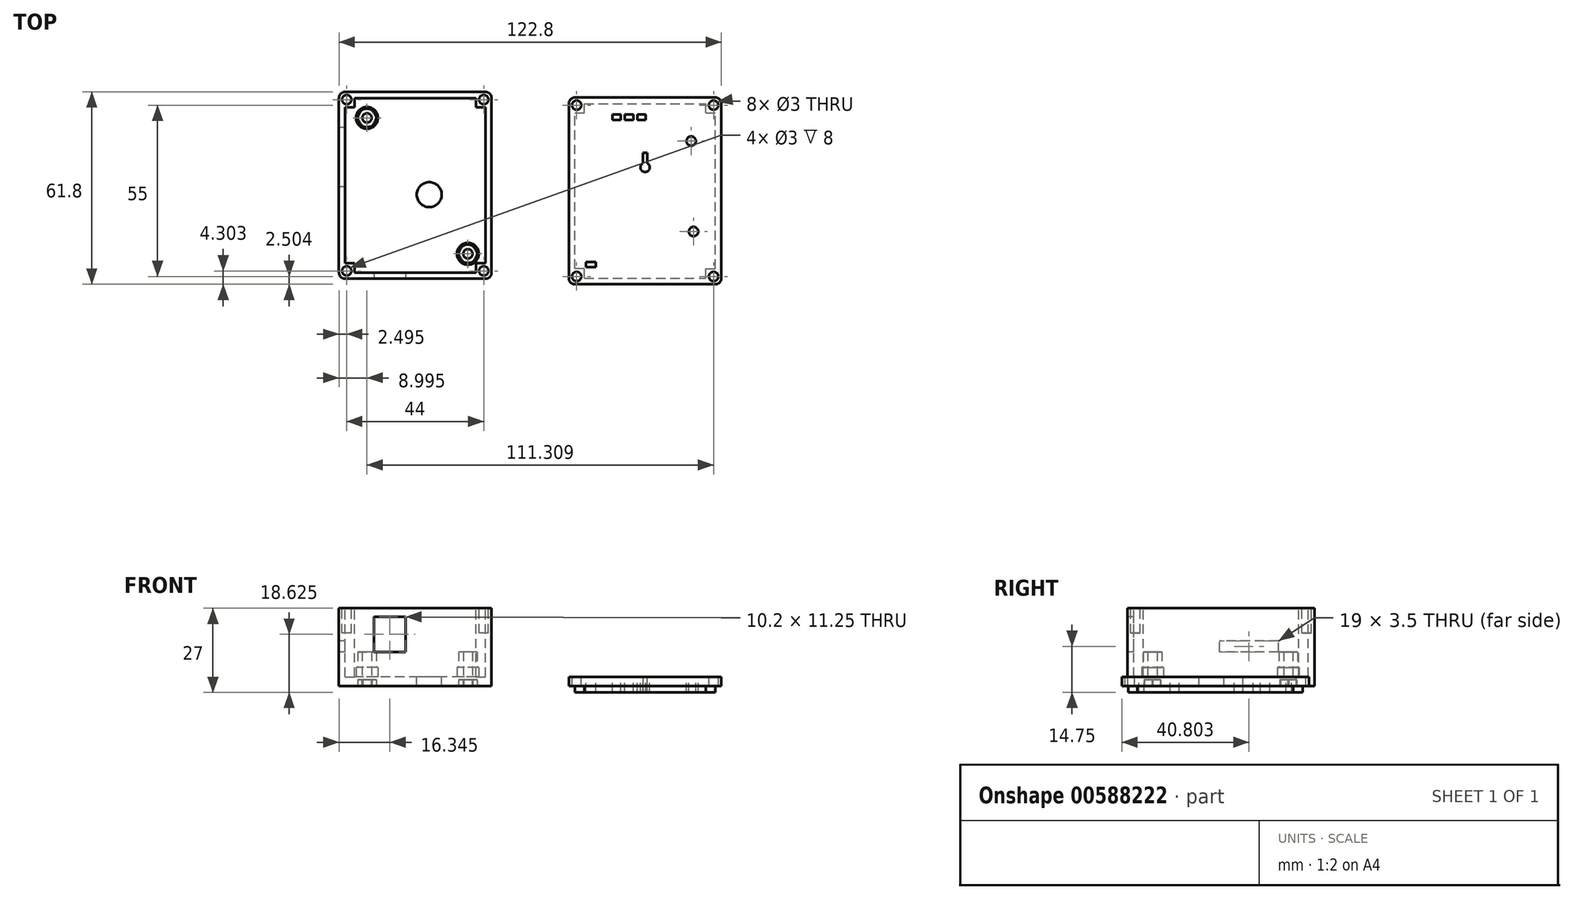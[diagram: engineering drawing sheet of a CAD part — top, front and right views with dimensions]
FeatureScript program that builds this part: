
annotation { "Feature Type Name" : "Feature", "Feature Type Description" : "" }
export const myFeature = defineFeature(function(context is Context, id is Id, definition is map)
    precondition{}
    {
        {
            var Q0;
            Q0=qCreatedBy(makeId("Top.planeOp"),FACE);
            var sketch = newSketch(context, id + "F0", { "sketchPlane" : qUnion([Q0])});
            skLineSegment(sketch, "E0.bottom", {"start": v(-66.77, 67.35) * mm, "end": v(-17.77, 67.35) * mm});
            skLineSegment(sketch, "E0.top", {"start": v(-66.77, 7.35) * mm, "end": v(-17.77, 7.35) * mm});
            skLineSegment(sketch, "E0.left", {"start": v(-66.77, 67.35) * mm, "end": v(-66.77, 7.35) * mm});
            skLineSegment(sketch, "E0.right", {"start": v(-17.77, 67.35) * mm, "end": v(-17.77, 7.35) * mm});
            skPoint(sketch, "E1.middle", {"position": v(-42.27, 37.35) * mm});
            skPoint(sketch, "E1.middle.positionSnap0", {"position": v(-66.77, 37.35) * mm});
            skPoint(sketch, "E1.middle.positionSnap1", {"position": v(-42.27, 67.35) * mm});
            skPoint(sketch, "E1.centerSnap0", {"position": v(-66.77, 37.35) * mm});
            skPoint(sketch, "E1.centerSnap1", {"position": v(-42.27, 67.35) * mm});
            skSolve(sketch);
        }
        {
            var Q0;
            Q0=makeQuery(id+"F0.imprint","IMPRINT",FACE,{"disambiguationData":[TD([[makeQuery(id+"F0.imprint","IMPRINT",EDGE,{"derivedFrom":sQuery(id+"F0.wireOp",EDGE,"E0.bottom")}),-1.0]])]});
            extrude(context, id + "F1", {"entities" : qUnion([Q0]), "depth" : 25 * mm, "offsetDistance" : 25 * mm});
        }
        {
            var Q0;
            Q0=makeQuery(id+"F1.opExtrude","CAP_FACE",FACE,{"disambiguationData":[OSD([sQuery(id+"F0.wireOp",EDGE,"E0.bottom"),sQuery(id+"F0.wireOp",EDGE,"E0.top"),sQuery(id+"F0.wireOp",EDGE,"E0.left"),sQuery(id+"F0.wireOp",EDGE,"E0.right")])],"isStart":false});
            var sketch = newSketch(context, id + "F2", { "sketchPlane" : qUnion([Q0])});
            skLineSegment(sketch, "E2.bottom", {"start": v(-61.77, 62.35) * mm, "end": v(-22.77, 62.35) * mm});
            skLineSegment(sketch, "E2.top", {"start": v(-61.77, 12.35) * mm, "end": v(-22.77, 12.35) * mm});
            skLineSegment(sketch, "E2.left", {"start": v(-61.77, 62.35) * mm, "end": v(-61.77, 12.35) * mm});
            skLineSegment(sketch, "E2.right", {"start": v(-22.77, 62.35) * mm, "end": v(-22.77, 12.35) * mm});
            skPoint(sketch, "E2.middle", {"position": v(-42.27, 37.35) * mm});
            skPoint(sketch, "E2.middle.positionSnap0", {"position": v(-17.77, 37.35) * mm});
            skPoint(sketch, "E2.middle.positionSnap1", {"position": v(-42.27, 67.35) * mm});
            skPoint(sketch, "E2.centerSnap0", {"position": v(-17.77, 37.35) * mm});
            skPoint(sketch, "E2.centerSnap1", {"position": v(-42.27, 67.35) * mm});
            skSolve(sketch);
        }
        {
            var Q0;
            Q0=makeQuery(id+"F2.imprint","IMPRINT",FACE,{"disambiguationData":[TD([[makeQuery(id+"F2.imprint","IMPRINT",EDGE,{"derivedFrom":sQuery(id+"F2.wireOp",EDGE,"E2.bottom")}),-1.0]])]});
            extrude(context, id + "F3", {"entities" : qUnion([Q0]), "operationType" : NewBodyOperationType.REMOVE, "oppositeDirection" : true, "depth" : 22 * mm, "offsetDistance" : 25 * mm});
        }
        {
            var Q0;
            Q0=makeQuery(id+"F1.opExtrude","CAP_FACE",FACE,{"disambiguationData":[OSD([sQuery(id+"F0.wireOp",EDGE,"E0.bottom"),sQuery(id+"F0.wireOp",EDGE,"E0.top"),sQuery(id+"F0.wireOp",EDGE,"E0.left"),sQuery(id+"F0.wireOp",EDGE,"E0.right")])],"isStart":false});
            var sketch = newSketch(context, id + "F4", { "sketchPlane" : qUnion([Q0])});
            skLineSegment(sketch, "E3.bottom", {"start": v(-61.77, 12.35) * mm, "end": v(-66.77, 12.35) * mm});
            skLineSegment(sketch, "E3.top", {"start": v(-61.77, 7.35) * mm, "end": v(-66.77, 7.35) * mm});
            skLineSegment(sketch, "E3.left", {"start": v(-61.77, 12.35) * mm, "end": v(-61.77, 7.35) * mm});
            skLineSegment(sketch, "E3.right", {"start": v(-66.77, 12.35) * mm, "end": v(-66.77, 7.35) * mm});
            skLineSegment(sketch, "E4.bottom", {"start": v(-22.77, 12.35) * mm, "end": v(-17.77, 12.35) * mm});
            skLineSegment(sketch, "E4.top", {"start": v(-22.77, 7.35) * mm, "end": v(-17.77, 7.35) * mm});
            skLineSegment(sketch, "E4.left", {"start": v(-22.77, 12.35) * mm, "end": v(-22.77, 7.35) * mm});
            skLineSegment(sketch, "E4.right", {"start": v(-17.77, 12.35) * mm, "end": v(-17.77, 7.35) * mm});
            skLineSegment(sketch, "E5.bottom", {"start": v(-61.77, 62.35) * mm, "end": v(-66.77, 62.35) * mm});
            skLineSegment(sketch, "E5.top", {"start": v(-61.77, 67.35) * mm, "end": v(-66.77, 67.35) * mm});
            skLineSegment(sketch, "E5.left", {"start": v(-61.77, 62.35) * mm, "end": v(-61.77, 67.35) * mm});
            skLineSegment(sketch, "E5.right", {"start": v(-66.77, 62.35) * mm, "end": v(-66.77, 67.35) * mm});
            skLineSegment(sketch, "E6.bottom", {"start": v(-22.77, 62.35) * mm, "end": v(-17.77, 62.35) * mm});
            skLineSegment(sketch, "E6.top", {"start": v(-22.77, 67.35) * mm, "end": v(-17.77, 67.35) * mm});
            skLineSegment(sketch, "E6.left", {"start": v(-22.77, 62.35) * mm, "end": v(-22.77, 67.35) * mm});
            skLineSegment(sketch, "E6.right", {"start": v(-17.77, 62.35) * mm, "end": v(-17.77, 67.35) * mm});
            skCircle(sketch, "E7", {"center": v(-64.27, 9.85) * mm, "radius": 1.5 * mm});
            skPoint(sketch, "E7.centerSnap0", {"position": v(-61.77, 9.85) * mm});
            skPoint(sketch, "E7.centerSnap1", {"position": v(-64.27, 12.35) * mm});
            skCircle(sketch, "E8", {"center": v(-64.27, 64.85) * mm, "radius": 1.5 * mm});
            skPoint(sketch, "E8.centerSnap0", {"position": v(-64.27, 62.35) * mm});
            skPoint(sketch, "E8.centerSnap1", {"position": v(-61.77, 64.85) * mm});
            skCircle(sketch, "E9", {"center": v(-20.27, 64.85) * mm, "radius": 1.5 * mm});
            skPoint(sketch, "E9.centerSnap0", {"position": v(-20.27, 62.35) * mm});
            skPoint(sketch, "E9.centerSnap1", {"position": v(-22.77, 64.85) * mm});
            skCircle(sketch, "E10", {"center": v(-20.27, 9.85) * mm, "radius": 1.5 * mm});
            skPoint(sketch, "E10.centerSnap0", {"position": v(-22.77, 9.85) * mm});
            skPoint(sketch, "E10.centerSnap1", {"position": v(-20.27, 12.35) * mm});
            skSolve(sketch);
        }
        {
            var Q0;
            Q0=makeQuery(id+"F4.imprint","IMPRINT",FACE,{"disambiguationData":[TD([[makeQuery(id+"F4.imprint","IMPRINT",EDGE,{"derivedFrom":sQuery(id+"F4.wireOp",EDGE,"E9")}),1.0]])]});
            var Q1;
            Q1=makeQuery(id+"F4.imprint","IMPRINT",FACE,{"disambiguationData":[TD([[makeQuery(id+"F4.imprint","IMPRINT",EDGE,{"derivedFrom":sQuery(id+"F4.wireOp",EDGE,"E10")}),1.0]])]});
            var Q2;
            Q2=makeQuery(id+"F4.imprint","IMPRINT",FACE,{"disambiguationData":[TD([[makeQuery(id+"F4.imprint","IMPRINT",EDGE,{"derivedFrom":sQuery(id+"F4.wireOp",EDGE,"E7")}),1.0]])]});
            var Q3;
            Q3=makeQuery(id+"F4.imprint","IMPRINT",FACE,{"disambiguationData":[TD([[makeQuery(id+"F4.imprint","IMPRINT",EDGE,{"derivedFrom":sQuery(id+"F4.wireOp",EDGE,"E8")}),1.0]])]});
            var Q4;
            Q4 = qSketchRegion(id + "F6", true);
            extrude(context, id + "F5", {"entities" : qUnion([Q0, Q1, Q2, Q3, Q4]), "operationType" : NewBodyOperationType.REMOVE, "oppositeDirection" : true, "depth" : 8 * mm, "offsetDistance" : 25 * mm});
        }
        {
            var Q0;
            Q0=makeQuery(id+"F1.opExtrude","CAP_FACE",FACE,{"disambiguationData":[OSD([sQuery(id+"F0.wireOp",EDGE,"E0.bottom"),sQuery(id+"F0.wireOp",EDGE,"E0.top"),sQuery(id+"F0.wireOp",EDGE,"E0.left"),sQuery(id+"F0.wireOp",EDGE,"E0.right")])],"isStart":false});
            var sketch = newSketch(context, id + "F6", { "sketchPlane" : qUnion([Q0])});
            skLineSegment(sketch, "E11.bottom", {"start": v(-22.77, 65.35) * mm, "end": v(-61.77, 65.35) * mm});
            skLineSegment(sketch, "E11.top", {"start": v(-22.77, 62.35) * mm, "end": v(-61.77, 62.35) * mm});
            skLineSegment(sketch, "E11.left", {"start": v(-22.77, 65.35) * mm, "end": v(-22.77, 62.35) * mm});
            skLineSegment(sketch, "E11.right", {"start": v(-61.77, 65.35) * mm, "end": v(-61.77, 62.35) * mm});
            skLineSegment(sketch, "E12.bottom", {"start": v(-22.77, 62.35) * mm, "end": v(-19.77, 62.35) * mm});
            skLineSegment(sketch, "E12.top", {"start": v(-22.77, 12.35) * mm, "end": v(-19.77, 12.35) * mm});
            skLineSegment(sketch, "E12.left", {"start": v(-22.77, 62.35) * mm, "end": v(-22.77, 12.35) * mm});
            skLineSegment(sketch, "E12.right", {"start": v(-19.77, 62.35) * mm, "end": v(-19.77, 12.35) * mm});
            skLineSegment(sketch, "E13.bottom", {"start": v(-61.77, 62.35) * mm, "end": v(-64.77, 62.35) * mm});
            skLineSegment(sketch, "E13.top", {"start": v(-61.77, 12.35) * mm, "end": v(-64.77, 12.35) * mm});
            skLineSegment(sketch, "E13.left", {"start": v(-61.77, 62.35) * mm, "end": v(-61.77, 12.35) * mm});
            skLineSegment(sketch, "E13.right", {"start": v(-64.77, 62.35) * mm, "end": v(-64.77, 12.35) * mm});
            skLineSegment(sketch, "E14.bottom", {"start": v(-22.77, 12.35) * mm, "end": v(-61.77, 12.35) * mm});
            skLineSegment(sketch, "E14.top", {"start": v(-22.77, 9.35) * mm, "end": v(-61.77, 9.35) * mm});
            skLineSegment(sketch, "E14.left", {"start": v(-22.77, 12.35) * mm, "end": v(-22.77, 9.35) * mm});
            skLineSegment(sketch, "E14.right", {"start": v(-61.77, 12.35) * mm, "end": v(-61.77, 9.35) * mm});
            skSolve(sketch);
        }
        {
            var Q0;
            Q0=makeQuery(id+"F6.imprint","IMPRINT",FACE,{"disambiguationData":[TD([[makeQuery(id+"F6.imprint","IMPRINT",EDGE,{"derivedFrom":sQuery(id+"F6.wireOp",EDGE,"E11.bottom")}),1.0]])]});
            var Q1;
            Q1=makeQuery(id+"F6.imprint","IMPRINT",FACE,{"disambiguationData":[TD([[makeQuery(id+"F6.imprint","IMPRINT",EDGE,{"derivedFrom":sQuery(id+"F6.wireOp",EDGE,"E13.bottom")}),1.0]])]});
            var Q2;
            Q2=makeQuery(id+"F6.imprint","IMPRINT",FACE,{"disambiguationData":[TD([[makeQuery(id+"F6.imprint","IMPRINT",EDGE,{"derivedFrom":sQuery(id+"F6.wireOp",EDGE,"E14.bottom")}),-1.0]])]});
            var Q3;
            Q3=makeQuery(id+"F6.imprint","IMPRINT",FACE,{"disambiguationData":[TD([[makeQuery(id+"F6.imprint","IMPRINT",EDGE,{"derivedFrom":sQuery(id+"F6.wireOp",EDGE,"E12.bottom")}),-1.0]])]});
            extrude(context, id + "F7", {"entities" : qUnion([Q0, Q1, Q2, Q3]), "operationType" : NewBodyOperationType.REMOVE, "oppositeDirection" : true, "depth" : 22 * mm, "offsetDistance" : 25 * mm});
        }
        {
            var Q0;
            Q0=makeQuery(id+"F7.boolean.opBoolean","MERGE",FACE,{"derivedFrom":[makeQuery(id+"F3.boolean.opBoolean","COPY",FACE,{"derivedFrom":makeQuery(id+"F3.opExtrude","CAP_FACE",FACE,{"disambiguationData":[OSD([sQuery(id+"F2.wireOp",EDGE,"E2.bottom"),sQuery(id+"F2.wireOp",EDGE,"E2.top"),sQuery(id+"F2.wireOp",EDGE,"E2.left"),sQuery(id+"F2.wireOp",EDGE,"E2.right")])],"isStart":false})}),makeQuery(id+"F7.opExtrude","CAP_FACE",FACE,{"disambiguationData":[OSD([sQuery(id+"F6.wireOp",EDGE,"E11.bottom"),sQuery(id+"F6.wireOp",EDGE,"E11.top"),sQuery(id+"F6.wireOp",EDGE,"E11.left"),sQuery(id+"F6.wireOp",EDGE,"E11.right")])],"isStart":false}),makeQuery(id+"F7.opExtrude","CAP_FACE",FACE,{"disambiguationData":[OSD([sQuery(id+"F6.wireOp",EDGE,"E12.bottom"),sQuery(id+"F6.wireOp",EDGE,"E12.top"),sQuery(id+"F6.wireOp",EDGE,"E12.left"),sQuery(id+"F6.wireOp",EDGE,"E12.right")])],"isStart":false}),makeQuery(id+"F7.opExtrude","CAP_FACE",FACE,{"disambiguationData":[OSD([sQuery(id+"F6.wireOp",EDGE,"E13.bottom"),sQuery(id+"F6.wireOp",EDGE,"E13.top"),sQuery(id+"F6.wireOp",EDGE,"E13.left"),sQuery(id+"F6.wireOp",EDGE,"E13.right")])],"isStart":false}),makeQuery(id+"F7.opExtrude","CAP_FACE",FACE,{"disambiguationData":[OSD([sQuery(id+"F6.wireOp",EDGE,"E14.bottom"),sQuery(id+"F6.wireOp",EDGE,"E14.top"),sQuery(id+"F6.wireOp",EDGE,"E14.left"),sQuery(id+"F6.wireOp",EDGE,"E14.right")])],"isStart":false})]});
            var sketch = newSketch(context, id + "F8", { "sketchPlane" : qUnion([Q0])});
            skCircle(sketch, "E15", {"center": v(-57.77, 58.97) * mm, "radius": 3 * mm});
            skCircle(sketch, "E16", {"center": v(-57.77, 58.97) * mm, "radius": 1.5 * mm});
            skCircle(sketch, "E17", {"center": v(-25.37, 15.35) * mm, "radius": 1.5 * mm});
            skCircle(sketch, "E18", {"center": v(-25.37, 15.35) * mm, "radius": 3 * mm});
            skSolve(sketch);
        }
        {
            var Q0;
            Q0=makeQuery(id+"F8.imprint","IMPRINT",FACE,{"disambiguationData":[TD([[makeQuery(id+"F8.imprint","IMPRINT",EDGE,{"derivedFrom":sQuery(id+"F8.wireOp",EDGE,"E15")}),1.0]])]});
            var Q1;
            Q1=makeQuery(id+"F8.imprint","IMPRINT",FACE,{"disambiguationData":[TD([[makeQuery(id+"F8.imprint","IMPRINT",EDGE,{"derivedFrom":sQuery(id+"F8.wireOp",EDGE,"E17")}),-1.0]])]});
            extrude(context, id + "F9", {"entities" : qUnion([Q0, Q1]), "operationType" : NewBodyOperationType.ADD, "depth" : 8 * mm, "offsetDistance" : 25 * mm});
        }
        {
            var Q0;
            Q0=makeQuery(id+"F9.boolean.opBoolean","SPLIT",FACE,{"disambiguationData":[TD([makeQuery(id+"F9.opExtrude","SWEPT_FACE",FACE,{"disambiguationData":[OSD([sQuery(id+"F8.wireOp",EDGE,"E17")])]})])],"derivedFrom":makeQuery(id+"F7.boolean.opBoolean","MERGE",FACE,{"derivedFrom":[makeQuery(id+"F3.boolean.opBoolean","COPY",FACE,{"derivedFrom":makeQuery(id+"F3.opExtrude","CAP_FACE",FACE,{"disambiguationData":[OSD([sQuery(id+"F2.wireOp",EDGE,"E2.bottom"),sQuery(id+"F2.wireOp",EDGE,"E2.top"),sQuery(id+"F2.wireOp",EDGE,"E2.left"),sQuery(id+"F2.wireOp",EDGE,"E2.right")])],"isStart":false})}),makeQuery(id+"F7.opExtrude","CAP_FACE",FACE,{"disambiguationData":[OSD([sQuery(id+"F6.wireOp",EDGE,"E11.bottom"),sQuery(id+"F6.wireOp",EDGE,"E11.top"),sQuery(id+"F6.wireOp",EDGE,"E11.left"),sQuery(id+"F6.wireOp",EDGE,"E11.right")])],"isStart":false}),makeQuery(id+"F7.opExtrude","CAP_FACE",FACE,{"disambiguationData":[OSD([sQuery(id+"F6.wireOp",EDGE,"E12.bottom"),sQuery(id+"F6.wireOp",EDGE,"E12.top"),sQuery(id+"F6.wireOp",EDGE,"E12.left"),sQuery(id+"F6.wireOp",EDGE,"E12.right")])],"isStart":false}),makeQuery(id+"F7.opExtrude","CAP_FACE",FACE,{"disambiguationData":[OSD([sQuery(id+"F6.wireOp",EDGE,"E13.bottom"),sQuery(id+"F6.wireOp",EDGE,"E13.top"),sQuery(id+"F6.wireOp",EDGE,"E13.left"),sQuery(id+"F6.wireOp",EDGE,"E13.right")])],"isStart":false}),makeQuery(id+"F7.opExtrude","CAP_FACE",FACE,{"disambiguationData":[OSD([sQuery(id+"F6.wireOp",EDGE,"E14.bottom"),sQuery(id+"F6.wireOp",EDGE,"E14.top"),sQuery(id+"F6.wireOp",EDGE,"E14.left"),sQuery(id+"F6.wireOp",EDGE,"E14.right")])],"isStart":false})]})});
            var Q1;
            Q1=makeQuery(id+"F9.boolean.opBoolean","SPLIT",FACE,{"disambiguationData":[TD([makeQuery(id+"F9.opExtrude","SWEPT_FACE",FACE,{"disambiguationData":[OSD([sQuery(id+"F8.wireOp",EDGE,"E16")])]})])],"derivedFrom":makeQuery(id+"F7.boolean.opBoolean","MERGE",FACE,{"derivedFrom":[makeQuery(id+"F3.boolean.opBoolean","COPY",FACE,{"derivedFrom":makeQuery(id+"F3.opExtrude","CAP_FACE",FACE,{"disambiguationData":[OSD([sQuery(id+"F2.wireOp",EDGE,"E2.bottom"),sQuery(id+"F2.wireOp",EDGE,"E2.top"),sQuery(id+"F2.wireOp",EDGE,"E2.left"),sQuery(id+"F2.wireOp",EDGE,"E2.right")])],"isStart":false})}),makeQuery(id+"F7.opExtrude","CAP_FACE",FACE,{"disambiguationData":[OSD([sQuery(id+"F6.wireOp",EDGE,"E11.bottom"),sQuery(id+"F6.wireOp",EDGE,"E11.top"),sQuery(id+"F6.wireOp",EDGE,"E11.left"),sQuery(id+"F6.wireOp",EDGE,"E11.right")])],"isStart":false}),makeQuery(id+"F7.opExtrude","CAP_FACE",FACE,{"disambiguationData":[OSD([sQuery(id+"F6.wireOp",EDGE,"E12.bottom"),sQuery(id+"F6.wireOp",EDGE,"E12.top"),sQuery(id+"F6.wireOp",EDGE,"E12.left"),sQuery(id+"F6.wireOp",EDGE,"E12.right")])],"isStart":false}),makeQuery(id+"F7.opExtrude","CAP_FACE",FACE,{"disambiguationData":[OSD([sQuery(id+"F6.wireOp",EDGE,"E13.bottom"),sQuery(id+"F6.wireOp",EDGE,"E13.top"),sQuery(id+"F6.wireOp",EDGE,"E13.left"),sQuery(id+"F6.wireOp",EDGE,"E13.right")])],"isStart":false}),makeQuery(id+"F7.opExtrude","CAP_FACE",FACE,{"disambiguationData":[OSD([sQuery(id+"F6.wireOp",EDGE,"E14.bottom"),sQuery(id+"F6.wireOp",EDGE,"E14.top"),sQuery(id+"F6.wireOp",EDGE,"E14.left"),sQuery(id+"F6.wireOp",EDGE,"E14.right")])],"isStart":false})]})});
            extrude(context, id + "F10", {"entities" : qUnion([Q0, Q1]), "operationType" : NewBodyOperationType.REMOVE, "oppositeDirection" : true, "depth" : 11 * mm, "offsetDistance" : 25 * mm});
        }
        {
            var Q0;
            Q0=qCreatedBy(makeId("Top.planeOp"),FACE);
            var sketch = newSketch(context, id + "F11", { "sketchPlane" : qUnion([Q0])});
            skLineSegment(sketch, "E19.bottom", {"start": v(7.03, 65.55) * mm, "end": v(56.03, 65.55) * mm});
            skLineSegment(sketch, "E19.top", {"start": v(7.03, 5.55) * mm, "end": v(56.03, 5.55) * mm});
            skLineSegment(sketch, "E19.left", {"start": v(7.03, 65.55) * mm, "end": v(7.03, 5.55) * mm});
            skLineSegment(sketch, "E19.right", {"start": v(56.03, 65.55) * mm, "end": v(56.03, 5.55) * mm});
            skSolve(sketch);
        }
        {
            var Q0;
            Q0=makeQuery(id+"F11.imprint","IMPRINT",FACE,{"disambiguationData":[TD([[makeQuery(id+"F11.imprint","IMPRINT",EDGE,{"derivedFrom":sQuery(id+"F11.wireOp",EDGE,"E19.bottom")}),-1.0]])]});
            extrude(context, id + "F12", {"entities" : qUnion([Q0]), "depth" : 3 * mm, "offsetDistance" : 25 * mm});
        }
        {
            var Q0;
            Q0=makeQuery(id+"F12.opExtrude","CAP_FACE",FACE,{"disambiguationData":[OSD([sQuery(id+"F11.wireOp",EDGE,"E19.bottom"),sQuery(id+"F11.wireOp",EDGE,"E19.top"),sQuery(id+"F11.wireOp",EDGE,"E19.left"),sQuery(id+"F11.wireOp",EDGE,"E19.right")])],"isStart":false});
            var sketch = newSketch(context, id + "F13", { "sketchPlane" : qUnion([Q0])});
            skCircle(sketch, "E20", {"center": v(9.53, 63.05) * mm, "radius": 1.5 * mm});
            skCircle(sketch, "E21", {"center": v(53.53, 63.05) * mm, "radius": 1.5 * mm});
            skCircle(sketch, "E22", {"center": v(53.53, 8.05) * mm, "radius": 1.5 * mm});
            skCircle(sketch, "E23", {"center": v(9.53, 8.05) * mm, "radius": 1.5 * mm});
            skSolve(sketch);
        }
        {
            var Q0;
            Q0=makeQuery(id+"F13.imprint","IMPRINT",FACE,{"disambiguationData":[TD([[makeQuery(id+"F13.imprint","IMPRINT",EDGE,{"derivedFrom":sQuery(id+"F13.wireOp",EDGE,"E20")}),1.0]])]});
            var Q1;
            Q1=makeQuery(id+"F13.imprint","IMPRINT",FACE,{"disambiguationData":[TD([[makeQuery(id+"F13.imprint","IMPRINT",EDGE,{"derivedFrom":sQuery(id+"F13.wireOp",EDGE,"E21")}),1.0]])]});
            var Q2;
            Q2=makeQuery(id+"F13.imprint","IMPRINT",FACE,{"disambiguationData":[TD([[makeQuery(id+"F13.imprint","IMPRINT",EDGE,{"derivedFrom":sQuery(id+"F13.wireOp",EDGE,"E22")}),1.0]])]});
            var Q3;
            Q3=makeQuery(id+"F13.imprint","IMPRINT",FACE,{"disambiguationData":[TD([[makeQuery(id+"F13.imprint","IMPRINT",EDGE,{"derivedFrom":sQuery(id+"F13.wireOp",EDGE,"E23")}),1.0]])]});
            extrude(context, id + "F14", {"entities" : qUnion([Q0, Q1, Q2, Q3]), "operationType" : NewBodyOperationType.REMOVE, "oppositeDirection" : true, "depth" : 3 * mm, "offsetDistance" : 25 * mm});
        }
        {
            var Q0;
            Q0=makeQuery(id+"F1.opExtrude","SWEPT_FACE",FACE,{"disambiguationData":[OSD([sQuery(id+"F0.wireOp",EDGE,"E0.top")])]});
            var sketch = newSketch(context, id + "F15", { "sketchPlane" : qUnion([Q0])});
            skLineSegment(sketch, "E24.bottom", {"start": v(-66.77, 0) * mm, "end": v(-55.52, 0) * mm});
            skLineSegment(sketch, "E24.top", {"start": v(-66.77, 11) * mm, "end": v(-55.52, 11) * mm});
            skLineSegment(sketch, "E24.left", {"start": v(-66.77, 0) * mm, "end": v(-66.77, 11) * mm});
            skLineSegment(sketch, "E24.right", {"start": v(-55.52, 0) * mm, "end": v(-55.52, 11) * mm});
            skLineSegment(sketch, "E25.bottom", {"start": v(-55.52, 11) * mm, "end": v(-45.32, 11) * mm});
            skLineSegment(sketch, "E25.top", {"start": v(-55.52, 22.25) * mm, "end": v(-45.32, 22.25) * mm});
            skLineSegment(sketch, "E25.left", {"start": v(-55.52, 11) * mm, "end": v(-55.52, 22.25) * mm});
            skLineSegment(sketch, "E25.right", {"start": v(-45.32, 11) * mm, "end": v(-45.32, 22.25) * mm});
            skSolve(sketch);
        }
        {
            var Q0;
            Q0=makeQuery(id+"F15.imprint","IMPRINT",FACE,{"disambiguationData":[TD([[makeQuery(id+"F15.imprint","IMPRINT",EDGE,{"derivedFrom":sQuery(id+"F15.wireOp",EDGE,"E25.bottom")}),1.0]])]});
            extrude(context, id + "F16", {"entities" : qUnion([Q0]), "operationType" : NewBodyOperationType.REMOVE, "oppositeDirection" : true, "depth" : 2 * mm, "offsetDistance" : 25 * mm});
        }
        {
            var Q0;
            Q0=makeQuery(id+"F1.opExtrude","SWEPT_FACE",FACE,{"disambiguationData":[OSD([sQuery(id+"F0.wireOp",EDGE,"E0.left")])]});
            var sketch = newSketch(context, id + "F17", { "sketchPlane" : qUnion([Q0])});
            skLineSegment(sketch, "E26.bottom", {"start": v(-67.35, 0) * mm, "end": v(-55.85, 0) * mm});
            skLineSegment(sketch, "E26.top", {"start": v(-67.35, 11) * mm, "end": v(-55.85, 11) * mm});
            skLineSegment(sketch, "E26.left", {"start": v(-67.35, 0) * mm, "end": v(-67.35, 11) * mm});
            skLineSegment(sketch, "E26.right", {"start": v(-55.85, 0) * mm, "end": v(-55.85, 11) * mm});
            skLineSegment(sketch, "E27.bottom", {"start": v(-55.85, 11) * mm, "end": v(-36.85, 11) * mm});
            skLineSegment(sketch, "E27.top", {"start": v(-55.85, 14.5) * mm, "end": v(-36.85, 14.5) * mm});
            skLineSegment(sketch, "E27.left", {"start": v(-55.85, 11) * mm, "end": v(-55.85, 14.5) * mm});
            skLineSegment(sketch, "E27.right", {"start": v(-36.85, 11) * mm, "end": v(-36.85, 14.5) * mm});
            skSolve(sketch);
        }
        {
            var Q0;
            Q0=makeQuery(id+"F17.imprint","IMPRINT",FACE,{"disambiguationData":[TD([[makeQuery(id+"F17.imprint","IMPRINT",EDGE,{"derivedFrom":sQuery(id+"F17.wireOp",EDGE,"E27.bottom")}),1.0]])]});
            extrude(context, id + "F18", {"entities" : qUnion([Q0]), "operationType" : NewBodyOperationType.REMOVE, "oppositeDirection" : true, "depth" : 2 * mm, "offsetDistance" : 25 * mm});
        }
        {
            var Q0;
            {var subQ0=sQuery(id+"F6.wireOp",EDGE,"E12.right");var subQ1=sQuery(id+"F6.wireOp",EDGE,"E13.top");var subQ2=sQuery(id+"F6.wireOp",EDGE,"E14.top");var subQ3=sQuery(id+"F6.wireOp",EDGE,"E13.bottom");var subQ4=sQuery(id+"F6.wireOp",EDGE,"E11.right");var subQ5=sQuery(id+"F6.wireOp",EDGE,"E11.bottom");var subQ6=sQuery(id+"F2.wireOp",EDGE,"E2.bottom");var subQ7=sQuery(id+"F6.wireOp",EDGE,"E12.bottom");var subQ8=sQuery(id+"F2.wireOp",EDGE,"E2.top");var subQ9=sQuery(id+"F6.wireOp",EDGE,"E11.left");var subQ10=sQuery(id+"F6.wireOp",EDGE,"E12.top");var subQ11=sQuery(id+"F6.wireOp",EDGE,"E13.right");var subQ12=sQuery(id+"F6.wireOp",EDGE,"E14.left");var subQ13=sQuery(id+"F6.wireOp",EDGE,"E14.right");Q0=makeQuery(id+"F9.boolean.opBoolean","SPLIT",FACE,{"disambiguationData":[TD([makeQuery(id+"F3.boolean.opBoolean","COPY",FACE,{"derivedFrom":makeQuery(id+"F3.opExtrude","SWEPT_FACE",FACE,{"disambiguationData":[OSD([subQ6])]})})])],"derivedFrom":makeQuery(id+"F7.boolean.opBoolean","MERGE",FACE,{"derivedFrom":[makeQuery(id+"F3.boolean.opBoolean","COPY",FACE,{"derivedFrom":makeQuery(id+"F3.opExtrude","CAP_FACE",FACE,{"disambiguationData":[OSD([subQ6,subQ8,sQuery(id+"F2.wireOp",EDGE,"E2.left"),sQuery(id+"F2.wireOp",EDGE,"E2.right")])],"isStart":false})}),makeQuery(id+"F7.opExtrude","CAP_FACE",FACE,{"disambiguationData":[OSD([subQ5,sQuery(id+"F6.wireOp",EDGE,"E11.top"),subQ9,subQ4])],"isStart":false}),makeQuery(id+"F7.opExtrude","CAP_FACE",FACE,{"disambiguationData":[OSD([subQ7,subQ10,sQuery(id+"F6.wireOp",EDGE,"E12.left"),subQ0])],"isStart":false}),makeQuery(id+"F7.opExtrude","CAP_FACE",FACE,{"disambiguationData":[OSD([subQ3,subQ1,sQuery(id+"F6.wireOp",EDGE,"E13.left"),subQ11])],"isStart":false}),makeQuery(id+"F7.opExtrude","CAP_FACE",FACE,{"disambiguationData":[OSD([sQuery(id+"F6.wireOp",EDGE,"E14.bottom"),subQ2,subQ12,subQ13])],"isStart":false})]})});}
            var sketch = newSketch(context, id + "F19", { "sketchPlane" : qUnion([Q0])});
            skCircle(sketch, "E28", {"center": v(-57.77, 58.97) * mm, "radius": 3.5 * mm});
            skCircle(sketch, "E29", {"center": v(-25.37, 15.35) * mm, "radius": 3.5 * mm});
            skSolve(sketch);
        }
        {
            var Q0;
            Q0=makeQuery(id+"F19.imprint","IMPRINT",FACE,{"disambiguationData":[TD([[makeQuery(id+"F19.imprint","IMPRINT",EDGE,{"derivedFrom":sQuery(id+"F19.wireOp",EDGE,"E28")}),1.0]])]});
            var Q1;
            Q1=makeQuery(id+"F19.imprint","IMPRINT",FACE,{"disambiguationData":[TD([[makeQuery(id+"F19.imprint","IMPRINT",EDGE,{"derivedFrom":sQuery(id+"F19.wireOp",EDGE,"E29")}),1.0]])]});
            extrude(context, id + "F20", {"entities" : qUnion([Q0, Q1]), "operationType" : NewBodyOperationType.ADD, "depth" : 3 * mm, "offsetDistance" : 25 * mm});
        }
        {
            var Q0;
            Q0=makeQuery(id+"F1.opExtrude","CAP_FACE",FACE,{"disambiguationData":[OSD([sQuery(id+"F0.wireOp",EDGE,"E0.bottom"),sQuery(id+"F0.wireOp",EDGE,"E0.top"),sQuery(id+"F0.wireOp",EDGE,"E0.left"),sQuery(id+"F0.wireOp",EDGE,"E0.right")])],"isStart":true});
            var sketch = newSketch(context, id + "F21", { "sketchPlane" : qUnion([Q0])});
            skCircle(sketch, "E30", {"center": v(-57.77, -58.97) * mm, "radius": 3 * mm});
            skCircle(sketch, "E31", {"center": v(-25.37, -15.35) * mm, "radius": 3 * mm});
            skCircle(sketch, "E32.cCircle", {"center": v(-57.77, -58.97) * mm, "radius": 3 * mm, "construction": true});
            skLineSegment(sketch, "E32.0", {"start": v(-59.1, -56.28) * mm, "end": v(-56.1, -56.49) * mm});
            skLineSegment(sketch, "E32.1", {"start": v(-56.1, -56.49) * mm, "end": v(-54.78, -59.18) * mm});
            skLineSegment(sketch, "E32.2", {"start": v(-54.78, -59.18) * mm, "end": v(-56.46, -61.67) * mm});
            skLineSegment(sketch, "E32.3", {"start": v(-56.46, -61.67) * mm, "end": v(-59.45, -61.46) * mm});
            skLineSegment(sketch, "E32.4", {"start": v(-59.45, -61.46) * mm, "end": v(-60.77, -58.76) * mm});
            skLineSegment(sketch, "E32.5", {"start": v(-60.77, -58.76) * mm, "end": v(-59.1, -56.28) * mm});
            skCircle(sketch, "E33.cCircle", {"center": v(-25.37, -15.35) * mm, "radius": 3 * mm, "construction": true});
            skLineSegment(sketch, "E33.0", {"start": v(-26.74, -12.68) * mm, "end": v(-23.75, -12.83) * mm});
            skLineSegment(sketch, "E33.1", {"start": v(-23.75, -12.83) * mm, "end": v(-22.38, -15.5) * mm});
            skLineSegment(sketch, "E33.2", {"start": v(-22.38, -15.5) * mm, "end": v(-24, -18.02) * mm});
            skLineSegment(sketch, "E33.3", {"start": v(-24, -18.02) * mm, "end": v(-27, -17.87) * mm});
            skLineSegment(sketch, "E33.4", {"start": v(-27, -17.87) * mm, "end": v(-28.37, -15.2) * mm});
            skLineSegment(sketch, "E33.5", {"start": v(-28.37, -15.2) * mm, "end": v(-26.74, -12.68) * mm});
            skSolve(sketch);
        }
        {
            var Q0;
            Q0=makeQuery(id+"F21.imprint","IMPRINT",FACE,{"disambiguationData":[TD([[makeQuery(id+"F21.imprint","IMPRINT",EDGE,{"derivedFrom":sQuery(id+"F21.wireOp",EDGE,"E32.0")}),-1.0]])]});
            var Q1;
            Q1=makeQuery(id+"F21.imprint","IMPRINT",FACE,{"disambiguationData":[TD([[makeQuery(id+"F21.imprint","IMPRINT",EDGE,{"derivedFrom":sQuery(id+"F21.wireOp",EDGE,"E33.0")}),-1.0]])]});
            extrude(context, id + "F22", {"entities" : qUnion([Q0, Q1]), "operationType" : NewBodyOperationType.REMOVE, "oppositeDirection" : true, "depth" : 2 * mm, "offsetDistance" : 25 * mm});
        }
        {
            var Q0;
            {var subQ0=sQuery(id+"F6.wireOp",EDGE,"E12.right");var subQ1=sQuery(id+"F6.wireOp",EDGE,"E13.top");var subQ2=sQuery(id+"F6.wireOp",EDGE,"E14.top");var subQ3=sQuery(id+"F6.wireOp",EDGE,"E13.bottom");var subQ4=sQuery(id+"F6.wireOp",EDGE,"E11.right");var subQ5=sQuery(id+"F6.wireOp",EDGE,"E11.bottom");var subQ6=sQuery(id+"F2.wireOp",EDGE,"E2.bottom");var subQ7=sQuery(id+"F6.wireOp",EDGE,"E12.bottom");var subQ8=sQuery(id+"F2.wireOp",EDGE,"E2.top");var subQ9=sQuery(id+"F6.wireOp",EDGE,"E11.left");var subQ10=sQuery(id+"F6.wireOp",EDGE,"E12.top");var subQ11=sQuery(id+"F6.wireOp",EDGE,"E13.right");var subQ12=sQuery(id+"F6.wireOp",EDGE,"E14.left");var subQ13=sQuery(id+"F6.wireOp",EDGE,"E14.right");Q0=makeQuery(id+"F9.boolean.opBoolean","SPLIT",FACE,{"disambiguationData":[TD([makeQuery(id+"F3.boolean.opBoolean","COPY",FACE,{"derivedFrom":makeQuery(id+"F3.opExtrude","SWEPT_FACE",FACE,{"disambiguationData":[OSD([subQ6])]})})])],"derivedFrom":makeQuery(id+"F7.boolean.opBoolean","MERGE",FACE,{"derivedFrom":[makeQuery(id+"F3.boolean.opBoolean","COPY",FACE,{"derivedFrom":makeQuery(id+"F3.opExtrude","CAP_FACE",FACE,{"disambiguationData":[OSD([subQ6,subQ8,sQuery(id+"F2.wireOp",EDGE,"E2.left"),sQuery(id+"F2.wireOp",EDGE,"E2.right")])],"isStart":false})}),makeQuery(id+"F7.opExtrude","CAP_FACE",FACE,{"disambiguationData":[OSD([subQ5,sQuery(id+"F6.wireOp",EDGE,"E11.top"),subQ9,subQ4])],"isStart":false}),makeQuery(id+"F7.opExtrude","CAP_FACE",FACE,{"disambiguationData":[OSD([subQ7,subQ10,sQuery(id+"F6.wireOp",EDGE,"E12.left"),subQ0])],"isStart":false}),makeQuery(id+"F7.opExtrude","CAP_FACE",FACE,{"disambiguationData":[OSD([subQ3,subQ1,sQuery(id+"F6.wireOp",EDGE,"E13.left"),subQ11])],"isStart":false}),makeQuery(id+"F7.opExtrude","CAP_FACE",FACE,{"disambiguationData":[OSD([sQuery(id+"F6.wireOp",EDGE,"E14.bottom"),subQ2,subQ12,subQ13])],"isStart":false})]})});}
            var sketch = newSketch(context, id + "F23", { "sketchPlane" : qUnion([Q0])});
            skLineSegment(sketch, "E34.right", {"start": v(-22.77, 12.35) * mm, "end": v(-22.77, 34.35) * mm});
            skLineSegment(sketch, "E35.bottom", {"start": v(-22.77, 34.35) * mm, "end": v(-37.77, 34.35) * mm});
            skLineSegment(sketch, "E35.top", {"start": v(-22.77, 12.35) * mm, "end": v(-37.77, 12.35) * mm});
            skLineSegment(sketch, "E35.left", {"start": v(-22.77, 34.35) * mm, "end": v(-22.77, 12.35) * mm});
            skLineSegment(sketch, "E35.right", {"start": v(-37.77, 34.35) * mm, "end": v(-37.77, 12.35) * mm});
            skPoint(sketch, "E36.middle", {"position": v(-37.77, 34.35) * mm});
            skCircle(sketch, "E37", {"center": v(-37.77, 34.35) * mm, "radius": 4 * mm});
            skSolve(sketch);
        }
        {
            var Q0;
            {var subQ0=sQuery(id+"F23.wireOp",EDGE,"E35.right");var subQ1=sQuery(id+"F23.wireOp",EDGE,"E35.bottom");var subQ2=makeQuery(id+"F23.imprint","INTERSECT",VERTEX,{"derivedFrom":[subQ1,subQ0]});Q0=makeQuery(id+"F23.imprint","IMPRINT",FACE,{"disambiguationData":[TD([[makeQuery(id+"F23.imprint","IMPRINT",EDGE,{"disambiguationData":[TD([[subQ2,1.0]])],"derivedFrom":subQ1}),-1.0]])]});}
            var Q1;
            {var subQ0=sQuery(id+"F23.wireOp",EDGE,"E35.right");var subQ1=sQuery(id+"F23.wireOp",EDGE,"E35.bottom");var subQ2=makeQuery(id+"F23.imprint","INTERSECT",VERTEX,{"derivedFrom":[subQ1,subQ0]});Q1=makeQuery(id+"F23.imprint","IMPRINT",FACE,{"disambiguationData":[TD([[makeQuery(id+"F23.imprint","IMPRINT",EDGE,{"disambiguationData":[TD([[subQ2,1.0]])],"derivedFrom":subQ1}),1.0]])]});}
            extrude(context, id + "F24", {"entities" : qUnion([Q0, Q1]), "operationType" : NewBodyOperationType.REMOVE, "oppositeDirection" : true, "depth" : 3 * mm, "offsetDistance" : 25 * mm});
        }
        {
            var Q0;
            Q0=makeQuery(id+"F12.opExtrude","CAP_FACE",FACE,{"disambiguationData":[OSD([sQuery(id+"F11.wireOp",EDGE,"E19.bottom"),sQuery(id+"F11.wireOp",EDGE,"E19.top"),sQuery(id+"F11.wireOp",EDGE,"E19.left"),sQuery(id+"F11.wireOp",EDGE,"E19.right")])],"isStart":false});
            var sketch = newSketch(context, id + "F25", { "sketchPlane" : qUnion([Q0])});
            skLineSegment(sketch, "E38.bottom", {"start": v(21.03, 60.05) * mm, "end": v(23.73, 60.05) * mm});
            skLineSegment(sketch, "E38.top", {"start": v(21.03, 58.25) * mm, "end": v(23.73, 58.25) * mm});
            skLineSegment(sketch, "E38.left", {"start": v(21.03, 60.05) * mm, "end": v(21.03, 58.25) * mm});
            skLineSegment(sketch, "E38.right", {"start": v(23.73, 60.05) * mm, "end": v(23.73, 58.25) * mm});
            skLineSegment(sketch, "E39.bottom", {"start": v(25.04, 60.05) * mm, "end": v(27.74, 60.05) * mm});
            skLineSegment(sketch, "E39.top", {"start": v(25.04, 58.25) * mm, "end": v(27.74, 58.25) * mm});
            skLineSegment(sketch, "E39.left", {"start": v(25.04, 60.05) * mm, "end": v(25.04, 58.25) * mm});
            skLineSegment(sketch, "E39.right", {"start": v(27.74, 60.05) * mm, "end": v(27.74, 58.25) * mm});
            skLineSegment(sketch, "E40.bottom", {"start": v(29.04, 60.05) * mm, "end": v(31.74, 60.05) * mm});
            skLineSegment(sketch, "E40.top", {"start": v(29.04, 58.25) * mm, "end": v(31.74, 58.25) * mm});
            skLineSegment(sketch, "E40.left", {"start": v(29.04, 60.05) * mm, "end": v(29.04, 58.25) * mm});
            skLineSegment(sketch, "E40.right", {"start": v(31.74, 60.05) * mm, "end": v(31.74, 58.25) * mm});
            skCircle(sketch, "E41", {"center": v(46.32, 51.55) * mm, "radius": 1.5 * mm});
            skCircle(sketch, "E42", {"center": v(47.08, 22.5) * mm, "radius": 1.5 * mm});
            skLineSegment(sketch, "E43.bottom", {"start": v(12.57, 12.7) * mm, "end": v(15.68, 12.7) * mm});
            skLineSegment(sketch, "E43.top", {"start": v(12.57, 11.01) * mm, "end": v(15.68, 11.01) * mm});
            skLineSegment(sketch, "E43.left", {"start": v(12.57, 12.7) * mm, "end": v(12.57, 11.01) * mm});
            skLineSegment(sketch, "E43.right", {"start": v(15.68, 12.7) * mm, "end": v(15.68, 11.01) * mm});
            skSolve(sketch);
        }
        {
            var Q0;
            Q0=makeQuery(id+"F25.imprint","IMPRINT",FACE,{"disambiguationData":[TD([[makeQuery(id+"F25.imprint","IMPRINT",EDGE,{"derivedFrom":sQuery(id+"F25.wireOp",EDGE,"E38.bottom")}),-1.0]])]});
            var Q1;
            Q1=makeQuery(id+"F25.imprint","IMPRINT",FACE,{"disambiguationData":[TD([[makeQuery(id+"F25.imprint","IMPRINT",EDGE,{"derivedFrom":sQuery(id+"F25.wireOp",EDGE,"E39.bottom")}),-1.0]])]});
            var Q2;
            Q2=makeQuery(id+"F25.imprint","IMPRINT",FACE,{"disambiguationData":[TD([[makeQuery(id+"F25.imprint","IMPRINT",EDGE,{"derivedFrom":sQuery(id+"F25.wireOp",EDGE,"E40.bottom")}),-1.0]])]});
            var Q3;
            Q3=makeQuery(id+"F25.imprint","IMPRINT",FACE,{"disambiguationData":[TD([[makeQuery(id+"F25.imprint","IMPRINT",EDGE,{"derivedFrom":sQuery(id+"F25.wireOp",EDGE,"E41")}),1.0]])]});
            var Q4;
            Q4=makeQuery(id+"F25.imprint","IMPRINT",FACE,{"disambiguationData":[TD([[makeQuery(id+"F25.imprint","IMPRINT",EDGE,{"derivedFrom":sQuery(id+"F25.wireOp",EDGE,"E42")}),1.0]])]});
            var Q5;
            Q5=makeQuery(id+"F25.imprint","IMPRINT",FACE,{"disambiguationData":[TD([[makeQuery(id+"F25.imprint","IMPRINT",EDGE,{"derivedFrom":sQuery(id+"F25.wireOp",EDGE,"E43.bottom")}),-1.0]])]});
            extrude(context, id + "F26", {"entities" : qUnion([Q0, Q1, Q2, Q3, Q4, Q5]), "operationType" : NewBodyOperationType.REMOVE, "oppositeDirection" : true, "depth" : 5 * mm, "offsetDistance" : 25 * mm});
        }
        {
            var Q0;
            Q0=makeQuery(id+"F12.opExtrude","CAP_FACE",FACE,{"disambiguationData":[OSD([sQuery(id+"F11.wireOp",EDGE,"E19.bottom"),sQuery(id+"F11.wireOp",EDGE,"E19.top"),sQuery(id+"F11.wireOp",EDGE,"E19.left"),sQuery(id+"F11.wireOp",EDGE,"E19.right")])],"isStart":false});
            var sketch = newSketch(context, id + "F27", { "sketchPlane" : qUnion([Q0])});
            skCircle(sketch, "E44", {"center": v(31.53, 43.1) * mm, "radius": 1.5 * mm});
            skLineSegment(sketch, "E45.bottom", {"start": v(32.28, 47.77) * mm, "end": v(30.78, 47.77) * mm});
            skLineSegment(sketch, "E45.left", {"start": v(32.28, 47.77) * mm, "end": v(32.28, 44.4) * mm});
            skLineSegment(sketch, "E45.right", {"start": v(30.78, 47.77) * mm, "end": v(30.78, 44.4) * mm});
            skPoint(sketch, "E45.middle", {"position": v(31.53, 46.09) * mm});
            skSolve(sketch);
        }
        {
            var Q0;
            Q0=makeQuery(id+"F27.imprint","IMPRINT",FACE,{"disambiguationData":[TD([[makeQuery(id+"F27.imprint","IMPRINT",EDGE,{"derivedFrom":sQuery(id+"F27.wireOp",EDGE,"E45.bottom")}),1.0]])]});
            var Q1;
            {var subQ0=sQuery(id+"F27.wireOp",EDGE,"E44");var subQ1=makeQuery(id+"F27.imprint","INTERSECT",VERTEX,{"derivedFrom":[subQ0,sQuery(id+"F27.wireOp",EDGE,"E45.left")]});Q1=makeQuery(id+"F27.imprint","IMPRINT",FACE,{"disambiguationData":[TD([[makeQuery(id+"F27.imprint","IMPRINT",EDGE,{"disambiguationData":[TD([[subQ1,-1.0]])],"derivedFrom":subQ0}),1.0]])]});}
            extrude(context, id + "F28", {"entities" : qUnion([Q0, Q1]), "operationType" : NewBodyOperationType.REMOVE, "oppositeDirection" : true, "depth" : 5 * mm, "offsetDistance" : 25 * mm});
        }
        {
            var Q0;
            Q0=makeQuery(id+"F1.opExtrude","SWEPT_EDGE",EDGE,{"disambiguationData":[OSD([sQuery(id+"F0.wireOp",EDGE,"E0.bottom"),sQuery(id+"F0.wireOp",EDGE,"E0.right")])]});
            var Q1;
            Q1=makeQuery(id+"F1.opExtrude","SWEPT_EDGE",EDGE,{"disambiguationData":[OSD([sQuery(id+"F0.wireOp",EDGE,"E0.top"),sQuery(id+"F0.wireOp",EDGE,"E0.right")])]});
            var Q2;
            Q2=makeQuery(id+"F1.opExtrude","SWEPT_EDGE",EDGE,{"disambiguationData":[OSD([sQuery(id+"F0.wireOp",EDGE,"E0.top"),sQuery(id+"F0.wireOp",EDGE,"E0.left")])]});
            var Q3;
            Q3=makeQuery(id+"F1.opExtrude","SWEPT_EDGE",EDGE,{"disambiguationData":[OSD([sQuery(id+"F0.wireOp",EDGE,"E0.bottom"),sQuery(id+"F0.wireOp",EDGE,"E0.left")])]});
            var Q4;
            Q4=makeQuery(id+"F12.opExtrude","SWEPT_EDGE",EDGE,{"disambiguationData":[OSD([sQuery(id+"F11.wireOp",EDGE,"E19.bottom"),sQuery(id+"F11.wireOp",EDGE,"E19.right")])]});
            var Q5;
            Q5=makeQuery(id+"F12.opExtrude","SWEPT_EDGE",EDGE,{"disambiguationData":[OSD([sQuery(id+"F11.wireOp",EDGE,"E19.top"),sQuery(id+"F11.wireOp",EDGE,"E19.right")])]});
            var Q6;
            Q6=makeQuery(id+"F12.opExtrude","SWEPT_EDGE",EDGE,{"disambiguationData":[OSD([sQuery(id+"F11.wireOp",EDGE,"E19.bottom"),sQuery(id+"F11.wireOp",EDGE,"E19.left")])]});
            var Q7;
            Q7=makeQuery(id+"F12.opExtrude","SWEPT_EDGE",EDGE,{"disambiguationData":[OSD([sQuery(id+"F11.wireOp",EDGE,"E19.top"),sQuery(id+"F11.wireOp",EDGE,"E19.left")])]});
            fillet(context, id + "F29", {"entities" : qUnion([Q0, Q1, Q2, Q3, Q4, Q5, Q6, Q7]), "radius" : 2 * mm, "tangentPropagation" : true, "allowEdgeOverflow" : false});
        }
        {
            var Q0;
            Q0=makeQuery(id+"F12.opExtrude","CAP_FACE",FACE,{"disambiguationData":[OSD([sQuery(id+"F11.wireOp",EDGE,"E19.bottom"),sQuery(id+"F11.wireOp",EDGE,"E19.top"),sQuery(id+"F11.wireOp",EDGE,"E19.left"),sQuery(id+"F11.wireOp",EDGE,"E19.right")])],"isStart":true});
            var sketch = newSketch(context, id + "F30", { "sketchPlane" : qUnion([Q0])});
            skLineSegment(sketch, "E46.bottom", {"start": v(12.03, -10.55) * mm, "end": v(51.03, -10.55) * mm});
            skLineSegment(sketch, "E46.top", {"start": v(12.03, -60.55) * mm, "end": v(51.03, -60.55) * mm});
            skLineSegment(sketch, "E46.left", {"start": v(12.03, -10.55) * mm, "end": v(12.03, -60.55) * mm});
            skLineSegment(sketch, "E46.right", {"start": v(51.03, -10.55) * mm, "end": v(51.03, -60.55) * mm});
            skPoint(sketch, "E46.middle", {"position": v(31.53, -35.55) * mm});
            skPoint(sketch, "E46.middle.positionSnap0", {"position": v(56.03, -35.55) * mm});
            skPoint(sketch, "E46.middle.positionSnap1", {"position": v(31.53, -65.55) * mm});
            skPoint(sketch, "E46.centerSnap0", {"position": v(56.03, -35.55) * mm});
            skPoint(sketch, "E46.centerSnap1", {"position": v(31.53, -65.55) * mm});
            skSolve(sketch);
        }
        {
            var Q0;
            Q0=makeQuery(id+"F30.imprint","IMPRINT",FACE,{"disambiguationData":[TD([[makeQuery(id+"F30.imprint","IMPRINT",EDGE,{"derivedFrom":sQuery(id+"F30.wireOp",EDGE,"E46.bottom")}),-1.0]])]});
            extrude(context, id + "F31", {"entities" : qUnion([Q0]), "operationType" : NewBodyOperationType.ADD, "depth" : 2 * mm, "offsetDistance" : 25 * mm});
        }
        {
            var Q0;
            Q0=makeQuery(id+"F12.opExtrude","CAP_FACE",FACE,{"disambiguationData":[OSD([sQuery(id+"F11.wireOp",EDGE,"E19.bottom"),sQuery(id+"F11.wireOp",EDGE,"E19.top"),sQuery(id+"F11.wireOp",EDGE,"E19.left"),sQuery(id+"F11.wireOp",EDGE,"E19.right")])],"isStart":true});
            var sketch = newSketch(context, id + "F32", { "sketchPlane" : qUnion([Q0])});
            skLineSegment(sketch, "E47.bottom", {"start": v(12.03, -10.55) * mm, "end": v(51.03, -10.55) * mm});
            skLineSegment(sketch, "E47.top", {"start": v(12.03, -7.55) * mm, "end": v(51.03, -7.55) * mm});
            skLineSegment(sketch, "E47.left", {"start": v(12.03, -10.55) * mm, "end": v(12.03, -7.55) * mm});
            skLineSegment(sketch, "E47.right", {"start": v(51.03, -10.55) * mm, "end": v(51.03, -7.55) * mm});
            skLineSegment(sketch, "E48.bottom", {"start": v(51.03, -10.55) * mm, "end": v(54.03, -10.55) * mm});
            skLineSegment(sketch, "E48.top", {"start": v(51.03, -60.55) * mm, "end": v(54.03, -60.55) * mm});
            skLineSegment(sketch, "E48.left", {"start": v(51.03, -10.55) * mm, "end": v(51.03, -60.55) * mm});
            skLineSegment(sketch, "E48.right", {"start": v(54.03, -10.55) * mm, "end": v(54.03, -60.55) * mm});
            skLineSegment(sketch, "E49.bottom", {"start": v(12.03, -10.55) * mm, "end": v(9.03, -10.55) * mm});
            skLineSegment(sketch, "E49.top", {"start": v(12.03, -60.55) * mm, "end": v(9.03, -60.55) * mm});
            skLineSegment(sketch, "E49.left", {"start": v(12.03, -10.55) * mm, "end": v(12.03, -60.55) * mm});
            skLineSegment(sketch, "E49.right", {"start": v(9.03, -10.55) * mm, "end": v(9.03, -60.55) * mm});
            skLineSegment(sketch, "E50.bottom", {"start": v(12.03, -60.55) * mm, "end": v(51.03, -60.55) * mm});
            skLineSegment(sketch, "E50.top", {"start": v(12.03, -63.55) * mm, "end": v(51.03, -63.55) * mm});
            skLineSegment(sketch, "E50.left", {"start": v(12.03, -60.55) * mm, "end": v(12.03, -63.55) * mm});
            skLineSegment(sketch, "E50.right", {"start": v(51.03, -60.55) * mm, "end": v(51.03, -63.55) * mm});
            skSolve(sketch);
        }
        {
            var Q0;
            Q0=makeQuery(id+"F32.imprint","IMPRINT",FACE,{"disambiguationData":[TD([[makeQuery(id+"F32.imprint","IMPRINT",EDGE,{"derivedFrom":sQuery(id+"F32.wireOp",EDGE,"E49.bottom")}),1.0]])]});
            var Q1;
            Q1=makeQuery(id+"F32.imprint","IMPRINT",FACE,{"disambiguationData":[TD([[makeQuery(id+"F32.imprint","IMPRINT",EDGE,{"derivedFrom":sQuery(id+"F32.wireOp",EDGE,"E47.bottom")}),1.0]])]});
            var Q2;
            Q2=makeQuery(id+"F32.imprint","IMPRINT",FACE,{"disambiguationData":[TD([[makeQuery(id+"F32.imprint","IMPRINT",EDGE,{"derivedFrom":sQuery(id+"F32.wireOp",EDGE,"E48.bottom")}),-1.0]])]});
            var Q3;
            Q3=makeQuery(id+"F32.imprint","IMPRINT",FACE,{"disambiguationData":[TD([[makeQuery(id+"F32.imprint","IMPRINT",EDGE,{"derivedFrom":sQuery(id+"F32.wireOp",EDGE,"E50.bottom")}),-1.0]])]});
            extrude(context, id + "F33", {"entities" : qUnion([Q0, Q1, Q2, Q3]), "operationType" : NewBodyOperationType.ADD, "depth" : 2 * mm, "offsetDistance" : 25 * mm});
        }
    });
